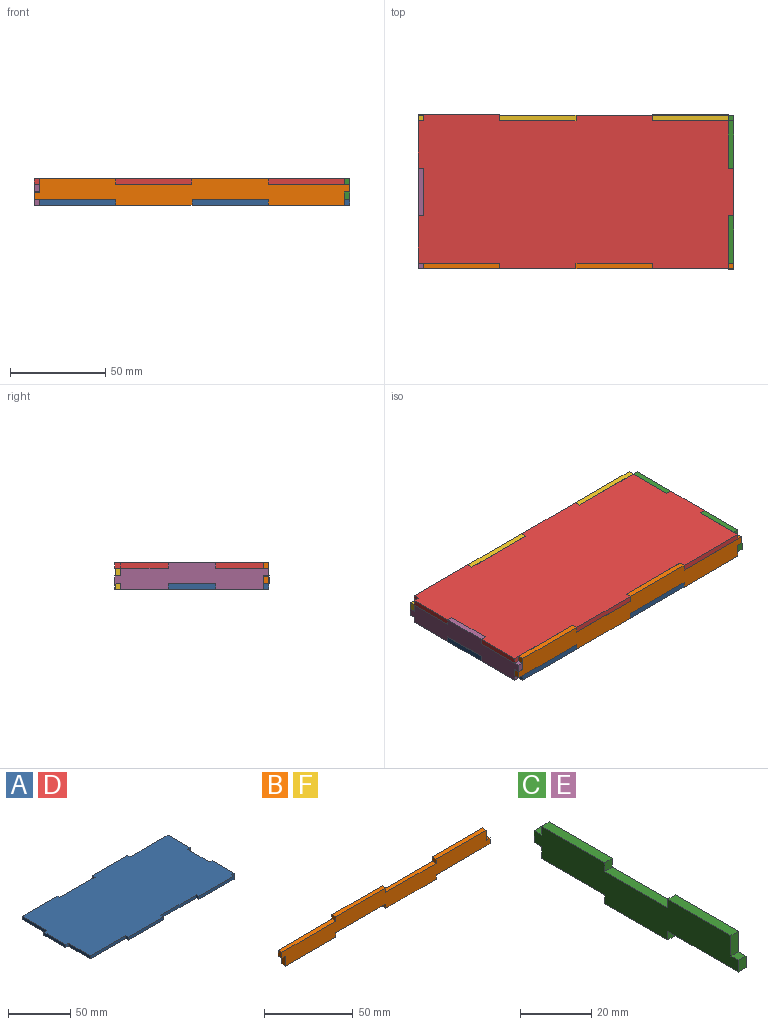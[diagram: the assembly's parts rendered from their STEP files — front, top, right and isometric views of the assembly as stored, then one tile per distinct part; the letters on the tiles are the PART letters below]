
ASSEMBLY  parts=6 mates=3
PART A: 28 faces, bbox 166x81x3 mm
  f0: plane 43x3mm, normal (0,1,0), area 129mm2, adj f1,f25,f26,f27
  f1: plane 3x3mm, normal (1,0,0), area 9mm2, adj f0,f2,f26,f27
  f2: plane 40x3mm, normal (0,1,0), area 120mm2, adj f1,f3,f26,f27
  f3: plane 3x3mm, normal (-1,0,0), area 9mm2, adj f2,f4,f26,f27
  f4: plane 40x3mm, normal (0,1,0), area 120mm2, adj f3,f5,f26,f27
  f5: plane 3x3mm, normal (1,0,0), area 9mm2, adj f4,f6,f26,f27
  f6: plane 40x3mm, normal (0,1,0), area 120mm2, adj f5,f7,f26,f27
  f7: plane 27.9x3mm, normal (-1,0,0), area 83.7mm2, adj f6,f8,f26,f27
  f8: plane 3x3mm, normal (0,1,0), area 9mm2, adj f7,f9,f26,f27
  f9: plane 25x3mm, normal (-1,0,0), area 75mm2, adj f8,f10,f26,f27
  f10: plane 3x3mm, normal (0,-1,0), area 9mm2, adj f9,f11,f26,f27
  f11: plane 25x3mm, normal (-1,0,0), area 75mm2, adj f10,f12,f26,f27
  f12: plane 40x3mm, normal (0,-1,0), area 120mm2, adj f11,f13,f26,f27
  f13: plane 3x3mm, normal (-1,0,0), area 9mm2, adj f12,f14,f26,f27
  f14: plane 40x3mm, normal (0,-1,0), area 120mm2, adj f13,f15,f26,f27
  f15: plane 3x3mm, normal (1,0,0), area 9mm2, adj f14,f16,f26,f27
  f16: plane 40x3mm, normal (0,-1,0), area 120mm2, adj f15,f17,f26,f27
  f17: plane 3.1x3mm, normal (-1,0,0), area 9.3mm2, adj f16,f18,f26,f27
  f18: plane 40x3mm, normal (0,-1,0), area 120mm2, adj f17,f19,f26,f27
  f19: plane 3x3mm, normal (1,0,0), area 9mm2, adj f18,f20,f26,f27
  f20: plane 3x3mm, normal (0,-1,0), area 9mm2, adj f19,f21,f26,f27
  f21: plane 25x3mm, normal (1,0,0), area 75mm2, adj f20,f22,f26,f27
  f22: plane 3x3mm, normal (0,1,0), area 9mm2, adj f21,f23,f26,f27
  f23: plane 25x3mm, normal (1,0,0), area 75mm2, adj f22,f24,f26,f27
  f24: plane 3x3mm, normal (0,-1,0), area 9mm2, adj f23,f25,f26,f27
  f25: plane 25x3mm, normal (1,0,0), area 75mm2, adj f0,f24,f26,f27
  f26: plane 166x81mm, normal (0,0,1), area 12693mm2, adj f0,f1,f2,f3,f4,f5,f6,f7
  f27: plane 166x81mm, normal (0,0,-1), area 12693mm2, adj f0,f1,f2,f3,f4,f5,f6,f7
PART B: 22 faces, bbox 166x3x14 mm
  f0: plane 7x3mm, normal (1,0,0), area 21mm2, adj f1,f19,f20,f21
  f1: plane 40x3mm, normal (0,0,1), area 120mm2, adj f0,f2,f20,f21
  f2: plane 3x3mm, normal (-1,0,0), area 9mm2, adj f1,f3,f20,f21
  f3: plane 40x3mm, normal (0,0,1), area 120mm2, adj f2,f4,f20,f21
  f4: plane 3x3mm, normal (1,0,0), area 9mm2, adj f3,f5,f20,f21
  f5: plane 40x3mm, normal (0,0,1), area 120mm2, adj f4,f6,f20,f21
  f6: plane 3x3mm, normal (-1,0,0), area 9mm2, adj f5,f7,f20,f21
  f7: plane 43x3mm, normal (0,0,1), area 129mm2, adj f6,f8,f20,f21
  f8: plane 4x3mm, normal (-1,0,0), area 12mm2, adj f7,f9,f20,f21
  f9: plane 3x3mm, normal (0,0,-1), area 9mm2, adj f8,f10,f20,f21
  f10: plane 7x3mm, normal (-1,0,0), area 21mm2, adj f9,f11,f20,f21
  f11: plane 40x3mm, normal (0,0,-1), area 120mm2, adj f10,f12,f20,f21
  f12: plane 3x3mm, normal (1,0,0), area 9mm2, adj f11,f13,f20,f21
  f13: plane 40x3mm, normal (0,0,-1), area 120mm2, adj f12,f14,f20,f21
  f14: plane 3x3mm, normal (-1,0,0), area 9mm2, adj f13,f15,f20,f21
  f15: plane 40x3mm, normal (0,0,-1), area 120mm2, adj f14,f16,f20,f21
  f16: plane 3x3mm, normal (1,0,0), area 9mm2, adj f15,f17,f20,f21
  f17: plane 43x3mm, normal (0,0,-1), area 129mm2, adj f16,f18,f20,f21
  f18: plane 4x3mm, normal (1,0,0), area 12mm2, adj f17,f19,f20,f21
  f19: plane 3x3mm, normal (0,0,1), area 9mm2, adj f0,f18,f20,f21
  f20: plane 166x14mm, normal (0,-1,0), area 1784mm2, adj f0,f1,f2,f3,f4,f5,f6,f7
  f21: plane 166x14mm, normal (0,1,0), area 1784mm2, adj f0,f1,f2,f3,f4,f5,f6,f7
PART C: 20 faces, bbox 3x81x14 mm
  f0: plane 7x3mm, normal (0,-1,0), area 21mm2, adj f1,f17,f18,f19
  f1: plane 3x3mm, normal (0,0,1), area 9mm2, adj f0,f2,f18,f19
  f2: plane 4x3mm, normal (0,-1,0), area 12mm2, adj f1,f3,f18,f19
  f3: plane 28x3mm, normal (0,0,-1), area 84mm2, adj f2,f4,f18,f19
  f4: plane 3x3mm, normal (0,-1,0), area 9mm2, adj f3,f5,f18,f19
  f5: plane 25x3mm, normal (0,0,-1), area 75mm2, adj f4,f6,f18,f19
  f6: plane 3x3mm, normal (0,1,0), area 9mm2, adj f5,f7,f18,f19
  f7: plane 25x3mm, normal (0,0,-1), area 75mm2, adj f6,f8,f18,f19
  f8: plane 4x3mm, normal (0,1,0), area 12mm2, adj f7,f9,f18,f19
  f9: plane 3x3mm, normal (0,0,-1), area 9mm2, adj f8,f10,f18,f19
  f10: plane 4x3mm, normal (0,1,0), area 12mm2, adj f9,f11,f18,f19
  f11: plane 3x3mm, normal (0,0,1), area 9mm2, adj f10,f12,f18,f19
  f12: plane 3x3mm, normal (0,1,0), area 9mm2, adj f11,f13,f18,f19
  f13: plane 25x3mm, normal (0,0,1), area 75mm2, adj f12,f14,f18,f19
  f14: plane 3x3mm, normal (0,-1,0), area 9mm2, adj f13,f15,f18,f19
  f15: plane 25x3mm, normal (0,0,1), area 75mm2, adj f14,f16,f18,f19
  f16: plane 3x3mm, normal (0,1,0), area 9mm2, adj f15,f17,f18,f19
  f17: plane 25x3mm, normal (0,0,1), area 75mm2, adj f0,f16,f18,f19
  f18: plane 81x14mm, normal (1,0,0), area 849mm2, adj f0,f1,f2,f3,f4,f5,f6,f7
  f19: plane 81x14mm, normal (-1,0,0), area 849mm2, adj f0,f1,f2,f3,f4,f5,f6,f7
PART D: same geometry as A
PART E: same geometry as C
PART F: same geometry as B
PLACE A rot(axis=(1,0,0),180deg) t=(2.69,13.05,-9.65)mm
PLACE B rot(axis=(1,0,0),180deg) t=(2.69,-67.95,-6.65)mm
PLACE C rot(axis=(0.94,0.34,0),0deg) t=(-0.31,12.9,-4.65)mm
PLACE D rot(axis=(0,0,1),180deg) t=(2.69,13,-1.65)mm
PLACE E rot(axis=(0,-1,0),180deg) t=(5.69,13,-6.65)mm
PLACE F t=(2.69,93.95,-4.65)mm
MATE fastened D.f17 <-> F.f6  axis (1,0,0) through (-37.31,51.95,-0.15)mm
MATE fastened C.f14 <-> D.f10  axis (0,-1,0) through (84.19,25.4,-0.15)mm
MATE fastened E.f4 <-> D.f24  axis (0,-1,0) through (-78.81,0.5,-0.15)mm
